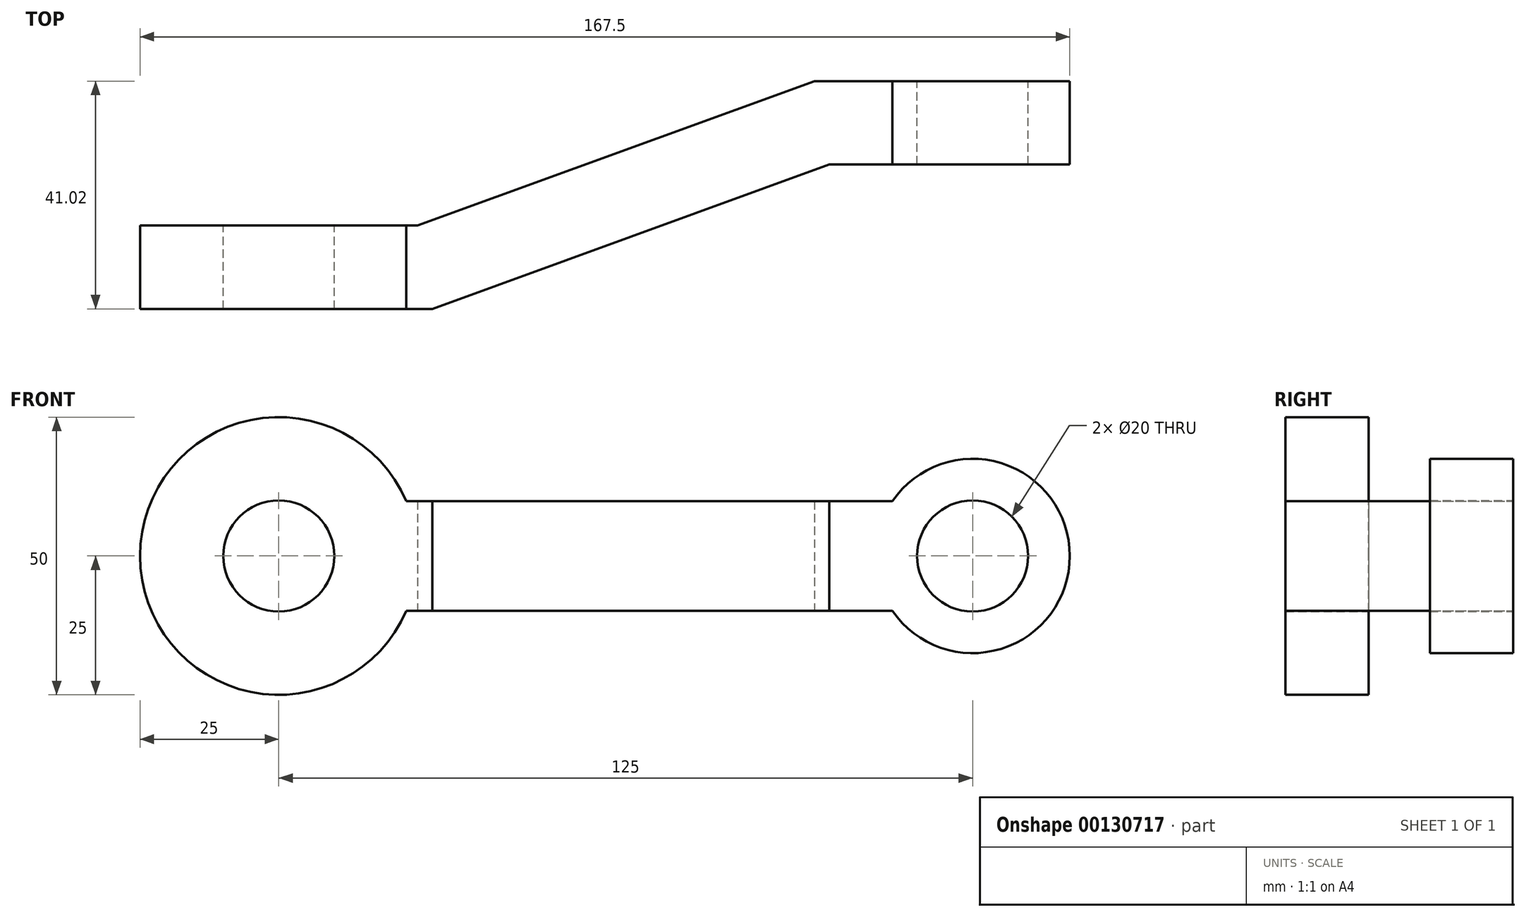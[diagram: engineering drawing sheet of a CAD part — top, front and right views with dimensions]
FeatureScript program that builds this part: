
annotation { "Feature Type Name" : "Feature", "Feature Type Description" : "" }
export const myFeature = defineFeature(function(context is Context, id is Id, definition is map)
    precondition{}
    {
        {
            var Q0;
            Q0=qCreatedBy(makeId("Front.planeOp"),FACE);
            var sketch = newSketch(context, id + "F0", { "sketchPlane" : qUnion([Q0])});
            skCircle(sketch, "E0", {"center": v(-59.93, 0) * mm, "radius": 25 * mm});
            skCircle(sketch, "E1", {"center": v(65.07, 0) * mm, "radius": 17.5 * mm});
            skCircle(sketch, "E2", {"center": v(-59.93, 0) * mm, "radius": 10 * mm});
            skCircle(sketch, "E3", {"center": v(65.07, 0) * mm, "radius": 10 * mm});
            skLineSegment(sketch, "E4", {"start": v(-36.96, 9.87) * mm, "end": v(50.62, 9.87) * mm});
            skLineSegment(sketch, "E5.MirrorCS", {"start": v(-36.96, -9.87) * mm, "end": v(50.62, -9.87) * mm});
            skSolve(sketch);
        }
        {
            var Q0;
            Q0 = qSketchRegion(id + "F0", true);
            var Q1;
            {var subQ0=sQuery(id+"F0.wireOp",EDGE,"E4");Q1=makeQuery(id+"F0.imprint","IMPRINT",FACE,{"disambiguationData":[TD([[makeQuery(id+"F0.imprint","IMPRINT",EDGE,{"derivedFrom":subQ0}),-1.0]])]});}
            extrude(context, id + "F1", {"entities" : qUnion([Q0, Q1]), "depth" : 25 * mm});
        }
        {
            var Q0;
            Q0=makeQuery(id+"F1.opExtrude","CAP_FACE",FACE,{"disambiguationData":[OSD([sQuery(id+"F0.wireOp",EDGE,"E0"),sQuery(id+"F0.wireOp",EDGE,"E1"),sQuery(id+"F0.wireOp",EDGE,"E2"),sQuery(id+"F0.wireOp",EDGE,"E3"),sQuery(id+"F0.wireOp",EDGE,"E4"),sQuery(id+"F0.wireOp",EDGE,"E5.MirrorCS")])],"isStart":false});
            extrude(context, id + "F2", {"entities" : qUnion([Q0]), "operationType" : NewBodyOperationType.ADD, "depth" : 25 * mm});
        }
        {
            var Q0;
            Q0=qCreatedBy(makeId("Top.planeOp"),FACE);
            var sketch = newSketch(context, id + "F3", { "sketchPlane" : qUnion([Q0])});
            skLineSegment(sketch, "E6", {"start": v(82.57, -2.39) * mm, "end": v(36.57, -2.39) * mm});
            skLineSegment(sketch, "E7", {"start": v(36.57, -2.39) * mm, "end": v(-34.93, -28.41) * mm});
            skLineSegment(sketch, "E8", {"start": v(-34.93, -28.41) * mm, "end": v(-84.93, -28.41) * mm});
            skLineSegment(sketch, "E9.0", {"start": v(-32.29, -43.41) * mm, "end": v(-84.93, -43.41) * mm});
            skLineSegment(sketch, "E9.1", {"start": v(39.21, -17.39) * mm, "end": v(-32.29, -43.41) * mm});
            skLineSegment(sketch, "E9.2", {"start": v(82.57, -17.39) * mm, "end": v(39.21, -17.39) * mm});
            skLineSegment(sketch, "E10", {"start": v(-84.93, -43.41) * mm, "end": v(-84.93, -28.41) * mm});
            skLineSegment(sketch, "E11", {"start": v(82.57, -2.39) * mm, "end": v(82.57, -17.39) * mm});
            skLineSegment(sketch, "E12", {"start": v(-84.93, -50) * mm, "end": v(-84.93, 0) * mm});
            skLineSegment(sketch, "E13", {"start": v(82.57, 0) * mm, "end": v(82.57, -50) * mm});
            skLineSegment(sketch, "E14", {"start": v(-84.93, -28.41) * mm, "end": v(-84.93, -43.41) * mm});
            skSolve(sketch);
        }
        {
            var Q0;
            Q0 = qSketchRegion(id + "F3", true);
            extrude(context, id + "F4", {"entities" : qUnion([Q0]), "operationType" : NewBodyOperationType.INTERSECT, "endBound" : BoundingType.SYMMETRIC, "depth" : 70 * mm});
        }
    });
